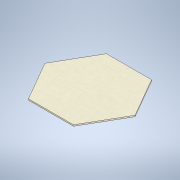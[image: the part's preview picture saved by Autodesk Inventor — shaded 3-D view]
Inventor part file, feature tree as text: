
AUTODESK INVENTOR PART (.ipt)
format: ipt  version: 2021 (Build 250183000, 183)  size: 101,376 bytes
history: native  units: mm
features: extrude x1, sketch x1
ambient origin geometry x8: Origin, YZ Plane, XZ Plane, XY Plane, X Axis, Y Axis, Z Axis, Center Point
bodies: Solid1 (feature_tree)
feature tree (2):
  extrude  "Extrusion1"  Depth=1.7mm TaperAngle=0.0deg
  sketch  "Sketch1"  dims[d0=101.0mm d1=1.7mm d2=0.0mm]
